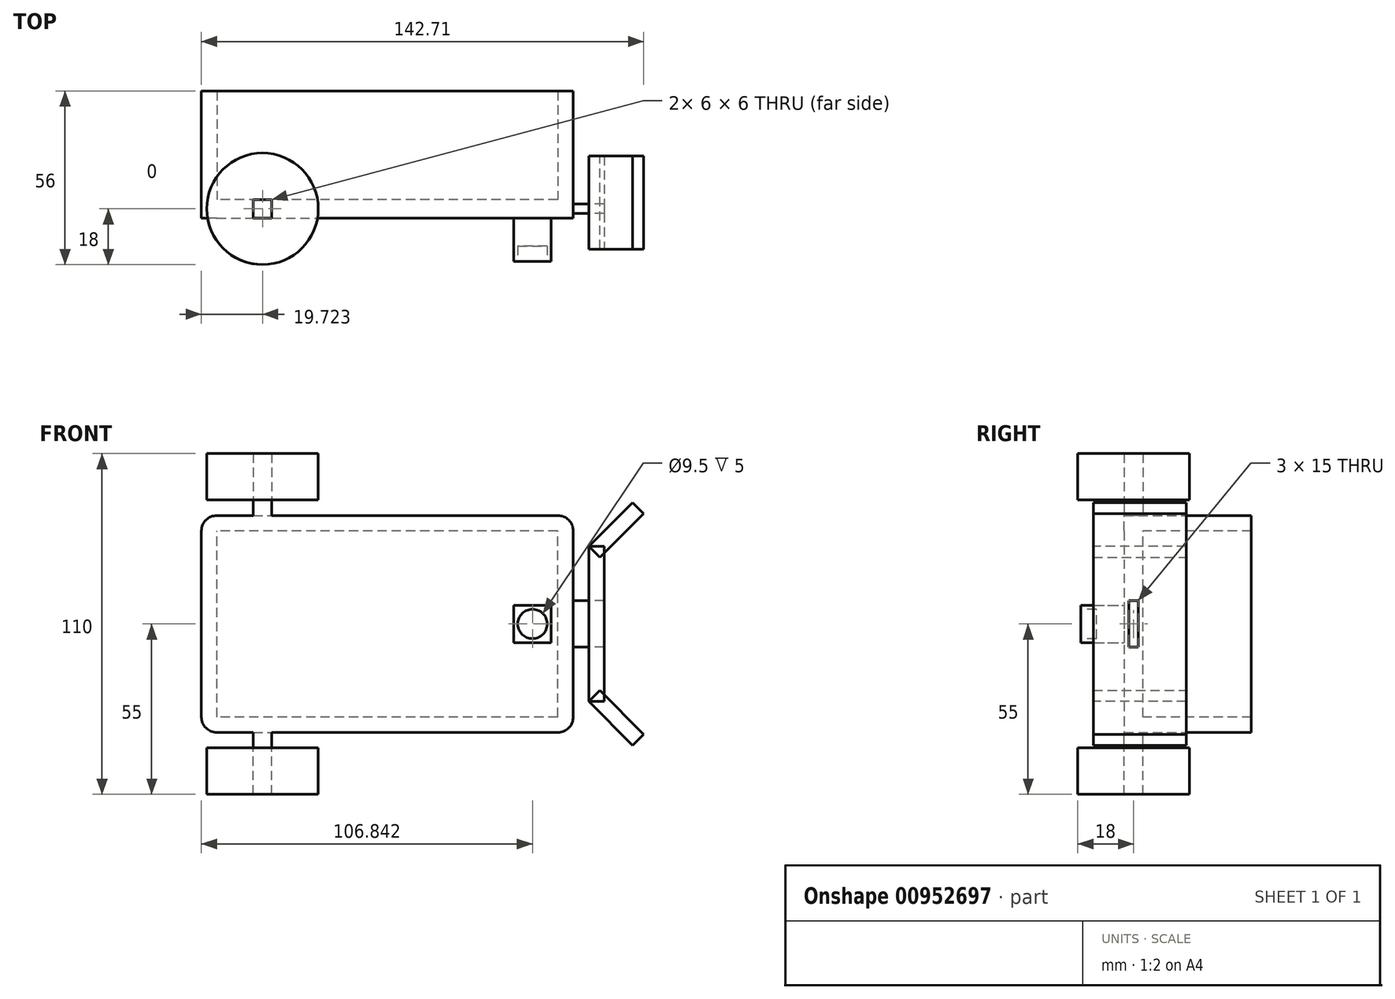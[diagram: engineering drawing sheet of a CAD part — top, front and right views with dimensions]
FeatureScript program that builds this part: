
annotation { "Feature Type Name" : "Feature", "Feature Type Description" : "" }
export const myFeature = defineFeature(function(context is Context, id is Id, definition is map)
    precondition{}
    {
        {
            var Q0;
            Q0=qCreatedBy(makeId("Front.planeOp"),FACE);
            var sketch = newSketch(context, id + "F0", { "sketchPlane" : qUnion([Q0])});
            skLineSegment(sketch, "E0.bottom", {"start": v(-55, 35) * mm, "end": v(55, 35) * mm});
            skLineSegment(sketch, "E0.top", {"start": v(-55, -35) * mm, "end": v(55, -35) * mm});
            skLineSegment(sketch, "E0.left", {"start": v(-60, 30) * mm, "end": v(-60, -30) * mm});
            skLineSegment(sketch, "E0.right", {"start": v(60, 30) * mm, "end": v(60, -30) * mm});
            skPoint(sketch, "E0.middle", {"position": v(0, 0) * mm});
            skPoint(sketch, "E1.visualSharp", {"position": v(-60, 35) * mm});
            skArc(sketch, "E1.filletArc", {"start": v(-55, 35) * mm, "mid": v(-58.54, 33.54) * mm, "end": v(-60, 30) * mm});
            skPoint(sketch, "E2.visualSharp", {"position": v(-60, -35) * mm});
            skArc(sketch, "E2.filletArc", {"start": v(-60, -30) * mm, "mid": v(-58.54, -33.54) * mm, "end": v(-55, -35) * mm});
            skPoint(sketch, "E3.visualSharp", {"position": v(60, -35) * mm});
            skArc(sketch, "E3.filletArc", {"start": v(55, -35) * mm, "mid": v(58.54, -33.54) * mm, "end": v(60, -30) * mm});
            skPoint(sketch, "E4.visualSharp", {"position": v(60, 35) * mm});
            skArc(sketch, "E4.filletArc", {"start": v(60, 30) * mm, "mid": v(58.54, 33.54) * mm, "end": v(55, 35) * mm});
            skSolve(sketch);
        }
        {
            var Q0;
            Q0=makeQuery(id+"F0.imprint","IMPRINT",FACE,{"disambiguationData":[TD([[makeQuery(id+"F0.imprint","IMPRINT",EDGE,{"derivedFrom":sQuery(id+"F0.wireOp",EDGE,"E0.bottom")}),-1.0]])]});
            extrude(context, id + "F1", {"entities" : qUnion([Q0]), "depth" : 6 * mm, "offsetDistance" : 25 * mm});
        }
        {
            var Q0;
            Q0=makeQuery(id+"F1.opExtrude","SWEPT_FACE",FACE,{"disambiguationData":[OSD([sQuery(id+"F0.wireOp",EDGE,"E0.top")])]});
            var sketch = newSketch(context, id + "F2", { "sketchPlane" : qUnion([Q0])});
            skLineSegment(sketch, "E5.bottom", {"start": v(-43.28, 6) * mm, "end": v(-37.28, 6) * mm});
            skLineSegment(sketch, "E5.top", {"start": v(-43.28, 0) * mm, "end": v(-37.28, 0) * mm});
            skLineSegment(sketch, "E5.left", {"start": v(-43.28, 6) * mm, "end": v(-43.28, 0) * mm});
            skLineSegment(sketch, "E5.right", {"start": v(-37.28, 6) * mm, "end": v(-37.28, 0) * mm});
            skSolve(sketch);
        }
        {
            var Q0;
            Q0=makeQuery(id+"F2.imprint","IMPRINT",FACE,{"disambiguationData":[TD([[makeQuery(id+"F2.imprint","IMPRINT",EDGE,{"derivedFrom":sQuery(id+"F2.wireOp",EDGE,"E5.bottom")}),-1.0]])]});
            var Q1;
            Q1=makeQuery(id+"F2.imprint","IMPRINT",FACE,{"disambiguationData":[TD([[makeQuery(id+"F2.imprint","IMPRINT",EDGE,{"derivedFrom":sQuery(id+"F2.wireOp",EDGE,"36b1ef66-63f0-49b3-a226-a5262a19ce8a0.MirrorCS")}),1.0]])]});
            extrude(context, id + "F3", {"entities" : qUnion([Q0, Q1]), "depth" : 5 * mm, "offsetDistance" : 25 * mm});
        }
        {
            var Q0;
            Q0=makeQuery(id+"F3.opExtrude","CAP_FACE",FACE,{"disambiguationData":[OSD([sQuery(id+"F2.wireOp",EDGE,"E5.bottom"),sQuery(id+"F2.wireOp",EDGE,"E5.top"),sQuery(id+"F2.wireOp",EDGE,"E5.left"),sQuery(id+"F2.wireOp",EDGE,"E5.right")])],"isStart":false});
            var sketch = newSketch(context, id + "F4", { "sketchPlane" : qUnion([Q0])});
            skLineSegment(sketch, "E6", {"start": v(-37.28, 3) * mm, "end": v(-40.28, 3) * mm});
            skPoint(sketch, "E6.endSnap0", {"position": v(-40.28, 6) * mm});
            skCircle(sketch, "E7", {"center": v(-40.28, 3) * mm, "radius": 18 * mm});
            skSolve(sketch);
        }
        {
            var Q0;
            Q0=makeQuery(id+"F4.imprint","IMPRINT",FACE,{"disambiguationData":[TD([[makeQuery(id+"F4.imprint","IMPRINT",EDGE,{"derivedFrom":sQuery(id+"F4.wireOp",EDGE,"E7")}),1.0]])]});
            var Q1;
            Q1=makeQuery(id+"F4.imprint","IMPRINT",FACE,{"disambiguationData":[TD([[makeQuery(id+"F4.imprint","IMPRINT",EDGE,{"derivedFrom":sQuery(id+"F4.wireOp",EDGE,"279cecf8-72cc-47d2-b7c5-359f4a76c95b0.MirrorC")}),-1.0]])]});
            extrude(context, id + "F5", {"entities" : qUnion([Q0, Q1]), "depth" : 15 * mm, "offsetDistance" : 25 * mm});
        }
        {
            var Q0;
            Q0=makeQuery(id+"F1.opExtrude","SWEPT_FACE",FACE,{"disambiguationData":[OSD([sQuery(id+"F0.wireOp",EDGE,"E0.bottom")])]});
            var sketch = newSketch(context, id + "F6", { "sketchPlane" : qUnion([Q0])});
            skLineSegment(sketch, "E8.bottom", {"start": v(-43.28, 0) * mm, "end": v(-37.28, 0) * mm});
            skLineSegment(sketch, "E8.top", {"start": v(-43.28, -6) * mm, "end": v(-37.28, -6) * mm});
            skLineSegment(sketch, "E8.left", {"start": v(-43.28, 0) * mm, "end": v(-43.28, -6) * mm});
            skLineSegment(sketch, "E8.right", {"start": v(-37.28, 0) * mm, "end": v(-37.28, -6) * mm});
            skSolve(sketch);
        }
        {
            var Q0;
            Q0=makeQuery(id+"F6.imprint","IMPRINT",FACE,{"disambiguationData":[TD([[makeQuery(id+"F6.imprint","IMPRINT",EDGE,{"derivedFrom":sQuery(id+"F6.wireOp",EDGE,"E8.bottom")}),-1.0]])]});
            var Q1;
            Q1=makeQuery(id+"F6.imprint","IMPRINT",FACE,{"disambiguationData":[TD([[makeQuery(id+"F6.imprint","IMPRINT",EDGE,{"derivedFrom":sQuery(id+"F6.wireOp",EDGE,"4da0a2db-94f4-45fb-9ec6-af3e451768c70.MirrorCS")}),1.0]])]});
            extrude(context, id + "F7", {"entities" : qUnion([Q0, Q1]), "depth" : 5 * mm, "offsetDistance" : 25 * mm});
        }
        {
            var Q0;
            Q0=makeQuery(id+"F7.opExtrude","CAP_FACE",FACE,{"disambiguationData":[OSD([sQuery(id+"F6.wireOp",EDGE,"E8.bottom"),sQuery(id+"F6.wireOp",EDGE,"E8.top"),sQuery(id+"F6.wireOp",EDGE,"E8.left"),sQuery(id+"F6.wireOp",EDGE,"E8.right")])],"isStart":false});
            var sketch = newSketch(context, id + "F8", { "sketchPlane" : qUnion([Q0])});
            skLineSegment(sketch, "E9", {"start": v(-43.28, -3) * mm, "end": v(-40.28, -3) * mm});
            skPoint(sketch, "E9.endSnap0", {"position": v(-40.28, 0) * mm});
            skCircle(sketch, "E10", {"center": v(-40.28, -3) * mm, "radius": 18 * mm});
            skSolve(sketch);
        }
        {
            var Q0;
            Q0=makeQuery(id+"F8.imprint","IMPRINT",FACE,{"disambiguationData":[TD([[makeQuery(id+"F8.imprint","IMPRINT",EDGE,{"derivedFrom":sQuery(id+"F8.wireOp",EDGE,"E10")}),1.0]])]});
            extrude(context, id + "F9", {"entities" : qUnion([Q0]), "depth" : 15 * mm, "offsetDistance" : 25 * mm});
        }
        {
            var Q0;
            Q0=makeQuery(id+"F1.opExtrude","CAP_FACE",FACE,{"disambiguationData":[OSD([sQuery(id+"F0.wireOp",EDGE,"E0.bottom"),sQuery(id+"F0.wireOp",EDGE,"E0.top"),sQuery(id+"F0.wireOp",EDGE,"E0.left"),sQuery(id+"F0.wireOp",EDGE,"E0.right"),sQuery(id+"F0.wireOp",EDGE,"E1.filletArc"),sQuery(id+"F0.wireOp",EDGE,"E2.filletArc"),sQuery(id+"F0.wireOp",EDGE,"E3.filletArc"),sQuery(id+"F0.wireOp",EDGE,"E4.filletArc")])],"isStart":false});
            var sketch = newSketch(context, id + "F10", { "sketchPlane" : qUnion([Q0])});
            skLineSegment(sketch, "E11.bottom", {"start": v(40.84, 6) * mm, "end": v(52.84, 6) * mm});
            skLineSegment(sketch, "E11.top", {"start": v(40.84, -6) * mm, "end": v(52.84, -6) * mm});
            skLineSegment(sketch, "E11.left", {"start": v(40.84, 6) * mm, "end": v(40.84, -6) * mm});
            skLineSegment(sketch, "E11.right", {"start": v(52.84, 6) * mm, "end": v(52.84, -6) * mm});
            skPoint(sketch, "E11.middle", {"position": v(46.84, 0) * mm});
            skSolve(sketch);
        }
        {
            var Q0;
            Q0=makeQuery(id+"F10.imprint","IMPRINT",FACE,{"disambiguationData":[TD([[makeQuery(id+"F10.imprint","IMPRINT",EDGE,{"derivedFrom":sQuery(id+"F10.wireOp",EDGE,"E11.bottom")}),-1.0]])]});
            extrude(context, id + "F11", {"entities" : qUnion([Q0]), "operationType" : NewBodyOperationType.ADD, "depth" : 14 * mm, "offsetDistance" : 25 * mm});
        }
        {
            var Q0;
            Q0=makeQuery(id+"F11.opExtrude","CAP_FACE",FACE,{"disambiguationData":[OSD([sQuery(id+"F10.wireOp",EDGE,"E11.bottom"),sQuery(id+"F10.wireOp",EDGE,"E11.top"),sQuery(id+"F10.wireOp",EDGE,"E11.left"),sQuery(id+"F10.wireOp",EDGE,"E11.right")])],"isStart":false});
            var sketch = newSketch(context, id + "F12", { "sketchPlane" : qUnion([Q0])});
            skCircle(sketch, "E12", {"center": v(46.84, 0) * mm, "radius": 4.75 * mm});
            skPoint(sketch, "E12.centerSnap0", {"position": v(46.84, 6) * mm});
            skSolve(sketch);
        }
        {
            var Q0;
            Q0=makeQuery(id+"F12.imprint","IMPRINT",FACE,{"disambiguationData":[TD([[makeQuery(id+"F12.imprint","IMPRINT",EDGE,{"derivedFrom":sQuery(id+"F12.wireOp",EDGE,"E12")}),1.0]])]});
            extrude(context, id + "F13", {"entities" : qUnion([Q0]), "operationType" : NewBodyOperationType.REMOVE, "oppositeDirection" : true, "depth" : 5 * mm, "offsetDistance" : 25 * mm});
        }
        {
            var Q0;
            Q0=makeQuery(id+"F1.opExtrude","SWEPT_FACE",FACE,{"disambiguationData":[OSD([sQuery(id+"F0.wireOp",EDGE,"E0.right")])]});
            var sketch = newSketch(context, id + "F14", { "sketchPlane" : qUnion([Q0])});
            skLineSegment(sketch, "E13.bottom", {"start": v(-1.5, 7.5) * mm, "end": v(-4.5, 7.5) * mm});
            skLineSegment(sketch, "E13.top", {"start": v(-1.5, -7.5) * mm, "end": v(-4.5, -7.5) * mm});
            skLineSegment(sketch, "E13.left", {"start": v(-1.5, 7.5) * mm, "end": v(-1.5, -7.5) * mm});
            skLineSegment(sketch, "E13.right", {"start": v(-4.5, 7.5) * mm, "end": v(-4.5, -7.5) * mm});
            skPoint(sketch, "E13.middle", {"position": v(-3, 0) * mm});
            skPoint(sketch, "E13.middle.positionSnap0", {"position": v(-3, 30) * mm});
            skPoint(sketch, "E13.centerSnap0", {"position": v(-3, 30) * mm});
            skSolve(sketch);
        }
        {
            var Q0;
            Q0=makeQuery(id+"F14.imprint","IMPRINT",FACE,{"disambiguationData":[TD([[makeQuery(id+"F14.imprint","IMPRINT",EDGE,{"derivedFrom":sQuery(id+"F14.wireOp",EDGE,"E13.bottom")}),1.0]])]});
            extrude(context, id + "F15", {"entities" : qUnion([Q0]), "operationType" : NewBodyOperationType.ADD, "depth" : 5 * mm, "offsetDistance" : 25 * mm});
        }
        {
            var Q0;
            Q0=makeQuery(id+"F15.opExtrude","CAP_FACE",FACE,{"disambiguationData":[OSD([sQuery(id+"F14.wireOp",EDGE,"E13.bottom"),sQuery(id+"F14.wireOp",EDGE,"E13.top"),sQuery(id+"F14.wireOp",EDGE,"E13.left"),sQuery(id+"F14.wireOp",EDGE,"E13.right")])],"isStart":false});
            var sketch = newSketch(context, id + "F16", { "sketchPlane" : qUnion([Q0])});
            skPoint(sketch, "E14.middle", {"position": v(-3, 0) * mm});
            skPoint(sketch, "E14.middle.positionSnap0", {"position": v(-3, 7.5) * mm});
            skPoint(sketch, "E14.centerSnap0", {"position": v(-3, 7.5) * mm});
            skLineSegment(sketch, "E15", {"start": v(14, 25) * mm, "end": v(-16, 25) * mm});
            skLineSegment(sketch, "E16", {"start": v(14, -25) * mm, "end": v(-16, -25) * mm});
            skLineSegment(sketch, "E17", {"start": v(-16, 25) * mm, "end": v(-16, -25) * mm});
            skLineSegment(sketch, "E18", {"start": v(14, 25) * mm, "end": v(14, -25) * mm});
            skSolve(sketch);
        }
        {
            var Q0;
            Q0=makeQuery(id+"F16.imprint","IMPRINT",FACE,{"disambiguationData":[TD([[makeQuery(id+"F16.imprint","IMPRINT",EDGE,{"derivedFrom":sQuery(id+"F16.wireOp",EDGE,"E15")}),1.0]])]});
            extrude(context, id + "F17", {"entities" : qUnion([Q0]), "depth" : 5 * mm, "offsetDistance" : 25 * mm});
        }
        {
            var Q0;
            Q0=makeQuery(id+"F17.opExtrude","CAP_FACE",FACE,{"disambiguationData":[OSD([sQuery(id+"F14.wireOp",EDGE,"E13.bottom"),sQuery(id+"F14.wireOp",EDGE,"E13.top"),sQuery(id+"F14.wireOp",EDGE,"E13.left"),sQuery(id+"F14.wireOp",EDGE,"E13.right"),sQuery(id+"F16.wireOp",EDGE,"E15"),sQuery(id+"F16.wireOp",EDGE,"E16"),sQuery(id+"F16.wireOp",EDGE,"E17"),sQuery(id+"F16.wireOp",EDGE,"E18")])],"isStart":false});
            var sketch = newSketch(context, id + "F18", { "sketchPlane" : qUnion([Q0])});
            skLineSegment(sketch, "E19.bottom", {"start": v(-16, 25) * mm, "end": v(14, 25) * mm});
            skLineSegment(sketch, "E19.top", {"start": v(-16, 20) * mm, "end": v(14, 20) * mm});
            skLineSegment(sketch, "E19.left", {"start": v(-16, 25) * mm, "end": v(-16, 20) * mm});
            skLineSegment(sketch, "E19.right", {"start": v(14, 25) * mm, "end": v(14, 20) * mm});
            skLineSegment(sketch, "E20.MirrorCS", {"start": v(-16, -20) * mm, "end": v(14, -20) * mm});
            skLineSegment(sketch, "E21.MirrorCS", {"start": v(-16, -25) * mm, "end": v(-16, -20) * mm});
            skLineSegment(sketch, "E22.MirrorCS", {"start": v(-16, -25) * mm, "end": v(14, -25) * mm});
            skLineSegment(sketch, "E23.MirrorCS", {"start": v(14, -25) * mm, "end": v(14, -20) * mm});
            skSolve(sketch);
        }
        {
            var Q0;
            Q0=makeQuery(id+"F18.imprint","IMPRINT",FACE,{"disambiguationData":[TD([[makeQuery(id+"F18.imprint","IMPRINT",EDGE,{"derivedFrom":sQuery(id+"F18.wireOp",EDGE,"E19.bottom")}),1.0]])]});
            var Q1;
            Q1=makeQuery(id+"F18.imprint","IMPRINT",FACE,{"disambiguationData":[TD([[makeQuery(id+"F18.imprint","IMPRINT",EDGE,{"derivedFrom":sQuery(id+"F18.wireOp",EDGE,"E20.MirrorCS")}),-1.0]])]});
            extrude(context, id + "F19", {"entities" : qUnion([Q0, Q1]), "depth" : 20 * mm, "offsetDistance" : 25 * mm});
        }
        {
            var Q0;
            Q0=makeQuery(id+"F19.opExtrude","SWEPT_BODY",BODY,{"disambiguationData":[OSD([sQuery(id+"F18.wireOp",EDGE,"E19.bottom"),sQuery(id+"F18.wireOp",EDGE,"E19.top"),sQuery(id+"F18.wireOp",EDGE,"E19.left"),sQuery(id+"F18.wireOp",EDGE,"E19.right")])]});
            var Q1;
            Q1=makeQuery(id+"F17.opExtrude","CAP_EDGE",EDGE,{"disambiguationData":[OSD([sQuery(id+"F16.wireOp",EDGE,"E15")])],"isStart":false});
            transform(context, id + "F20", {"entities" : qUnion([Q0]), "transformType" : TransformType.ROTATION, "transformAxis" : qUnion([Q1]), "angle" : 45 * degree, "makeCopy" : false});
        }
        {
            var Q0;
            Q0=makeQuery(id+"F19.opExtrude","SWEPT_BODY",BODY,{"disambiguationData":[OSD([sQuery(id+"F18.wireOp",EDGE,"E19.bottom"),sQuery(id+"F18.wireOp",EDGE,"E19.top"),sQuery(id+"F18.wireOp",EDGE,"E19.left"),sQuery(id+"F18.wireOp",EDGE,"E19.right")])]});
            transform(context, id + "F21", {"entities" : qUnion([Q0]), "transformType" : TransformType.TRANSLATION_3D, "dx" : -4.97 * mm, "dy" : 0 * mm, "dz" : 0 * mm, "makeCopy" : false});
        }
        {
            var Q0;
            Q0=makeQuery(id+"F19.opExtrude","SWEPT_BODY",BODY,{"disambiguationData":[OSD([sQuery(id+"F18.wireOp",EDGE,"E20.MirrorCS"),sQuery(id+"F18.wireOp",EDGE,"E21.MirrorCS"),sQuery(id+"F18.wireOp",EDGE,"E22.MirrorCS"),sQuery(id+"F18.wireOp",EDGE,"E23.MirrorCS")])]});
            var Q1;
            Q1=makeQuery(id+"F17.opExtrude","CAP_EDGE",EDGE,{"disambiguationData":[OSD([sQuery(id+"F16.wireOp",EDGE,"E16")])],"isStart":false});
            var Q2;
            Q2=makeQuery(id+"F17.opExtrude","CAP_EDGE",EDGE,{"disambiguationData":[OSD([sQuery(id+"F16.wireOp",EDGE,"E16")])],"isStart":false});
            transform(context, id + "F22", {"entities" : qUnion([Q0]), "transformType" : TransformType.ROTATION, "transformAxis" : qUnion([Q2]), "angle" : 45 * degree, "oppositeDirection" : true, "makeCopy" : false});
        }
        {
            var Q0;
            Q0=makeQuery(id+"F19.opExtrude","SWEPT_BODY",BODY,{"disambiguationData":[OSD([sQuery(id+"F18.wireOp",EDGE,"E20.MirrorCS"),sQuery(id+"F18.wireOp",EDGE,"E21.MirrorCS"),sQuery(id+"F18.wireOp",EDGE,"E22.MirrorCS"),sQuery(id+"F18.wireOp",EDGE,"E23.MirrorCS")])]});
            transform(context, id + "F23", {"entities" : qUnion([Q0]), "transformType" : TransformType.TRANSLATION_3D, "dx" : -5 * mm, "dy" : 0 * mm, "dz" : 0 * mm, "makeCopy" : false});
        }
        {
            var Q0;
            Q0=makeQuery(id+"F1.opExtrude","CAP_FACE",FACE,{"disambiguationData":[OSD([sQuery(id+"F0.wireOp",EDGE,"E0.bottom"),sQuery(id+"F0.wireOp",EDGE,"E0.top"),sQuery(id+"F0.wireOp",EDGE,"E0.left"),sQuery(id+"F0.wireOp",EDGE,"E0.right"),sQuery(id+"F0.wireOp",EDGE,"E1.filletArc"),sQuery(id+"F0.wireOp",EDGE,"E2.filletArc"),sQuery(id+"F0.wireOp",EDGE,"E3.filletArc"),sQuery(id+"F0.wireOp",EDGE,"E4.filletArc")])],"isStart":true});
            var sketch = newSketch(context, id + "F24", { "sketchPlane" : qUnion([Q0])});
            skLineSegment(sketch, "E24.bottom", {"start": v(-55, 35) * mm, "end": v(55, 35) * mm});
            skLineSegment(sketch, "E24.top", {"start": v(-60, 30) * mm, "end": v(60, 30) * mm});
            skLineSegment(sketch, "E24.left", {"start": v(-60, 30) * mm, "end": v(-60, 30) * mm});
            skLineSegment(sketch, "E24.right", {"start": v(60, 30) * mm, "end": v(60, 30) * mm});
            skPoint(sketch, "E25.visualSharp", {"position": v(-60, 35) * mm});
            skArc(sketch, "E25.filletArc", {"start": v(-55, 35) * mm, "mid": v(-58.54, 33.54) * mm, "end": v(-60, 30) * mm});
            skPoint(sketch, "E26.visualSharp", {"position": v(60, 35) * mm});
            skArc(sketch, "E26.filletArc", {"start": v(60, 30) * mm, "mid": v(58.54, 33.54) * mm, "end": v(55, 35) * mm});
            skLineSegment(sketch, "E27.MirrorCS", {"start": v(-60, -30) * mm, "end": v(60, -30) * mm});
            skLineSegment(sketch, "E28.MirrorCS", {"start": v(-55, -35) * mm, "end": v(55, -35) * mm});
            skArc(sketch, "E29.MirrorCS", {"start": v(-55, -35) * mm, "mid": v(-58.54, -33.54) * mm, "end": v(-60, -30) * mm});
            skArc(sketch, "E30.MirrorCS", {"start": v(60, -30) * mm, "mid": v(58.54, -33.54) * mm, "end": v(55, -35) * mm});
            skLineSegment(sketch, "E31", {"start": v(-55, -30) * mm, "end": v(-55, 30) * mm});
            skLineSegment(sketch, "E32.MirrorCS", {"start": v(55, -30) * mm, "end": v(55, 30) * mm});
            skSolve(sketch);
        }
        {
            var Q0;
            Q0=makeQuery(id+"F24.imprint","IMPRINT",FACE,{"disambiguationData":[TD([[makeQuery(id+"F24.imprint","IMPRINT",EDGE,{"derivedFrom":sQuery(id+"F24.wireOp",EDGE,"E24.bottom")}),1.0]])]});
            var Q1;
            {var subQ2=sQuery(id+"F24.wireOp",EDGE,"E31");Q1=makeQuery(id+"F24.imprint","IMPRINT",FACE,{"disambiguationData":[TD([[makeQuery(id+"F24.imprint","IMPRINT",EDGE,{"derivedFrom":subQ2}),1.0]])]});}
            var Q2;
            Q2=makeQuery(id+"F24.imprint","IMPRINT",FACE,{"disambiguationData":[TD([[makeQuery(id+"F24.imprint","IMPRINT",EDGE,{"derivedFrom":sQuery(id+"F24.wireOp",EDGE,"E28.MirrorCS")}),-1.0]])]});
            var Q3;
            {var subQ2=sQuery(id+"F24.wireOp",EDGE,"E32.MirrorCS");Q3=makeQuery(id+"F24.imprint","IMPRINT",FACE,{"disambiguationData":[TD([[makeQuery(id+"F24.imprint","IMPRINT",EDGE,{"derivedFrom":subQ2}),-1.0]])]});}
            extrude(context, id + "F25", {"entities" : qUnion([Q0, Q1, Q2, Q3]), "operationType" : NewBodyOperationType.ADD, "depth" : 35 * mm, "offsetDistance" : 25 * mm});
        }
    });
